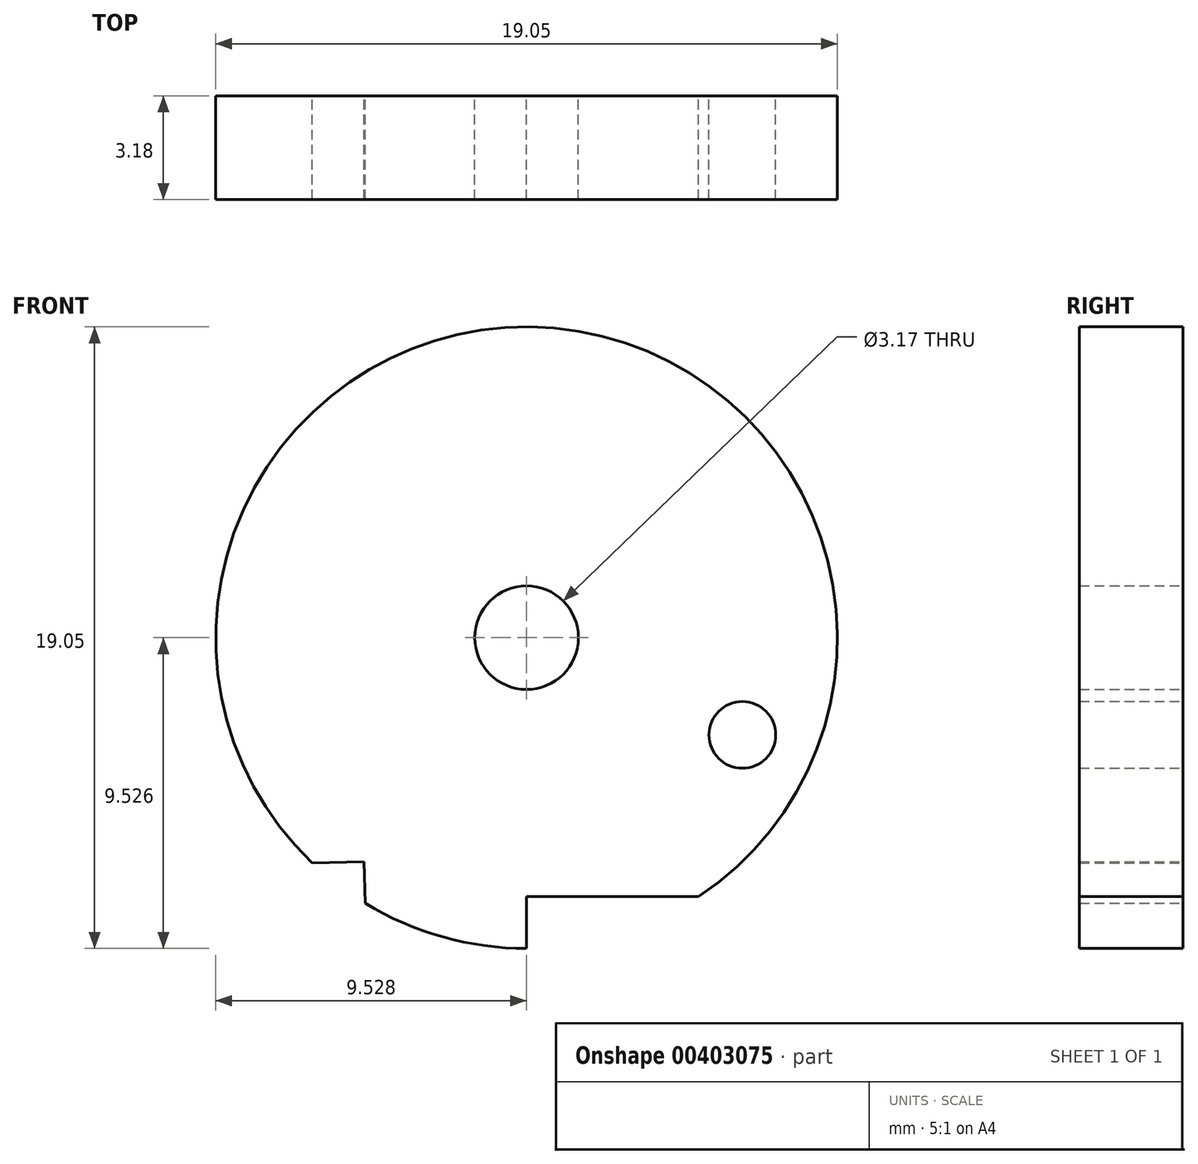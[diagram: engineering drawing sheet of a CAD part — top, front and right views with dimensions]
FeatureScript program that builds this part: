
annotation { "Feature Type Name" : "Feature", "Feature Type Description" : "" }
export const myFeature = defineFeature(function(context is Context, id is Id, definition is map)
    precondition{}
    {
        {
            var Q0;
            Q0=qCreatedBy(makeId("Front.planeOp"),FACE);
            var sketch = newSketch(context, id + "F0", { "sketchPlane" : qUnion([Q0])});
            skArc(sketch, "E0", {"start": v(-4.47, -3.05) * mm, "mid": v(-2.1, -4.09) * mm, "end": v(0.48, -4.44) * mm});
            skCircle(sketch, "E1", {"center": v(0.48, 5.09) * mm, "radius": 1.59 * mm});
            skLineSegment(sketch, "E2", {"start": v(-6.09, -1.81) * mm, "end": v(-4.5, -1.78) * mm});
            skLineSegment(sketch, "E3", {"start": v(-4.5, -1.78) * mm, "end": v(-4.47, -3.05) * mm});
            skCircle(sketch, "E4", {"center": v(7.09, 2.1) * mm, "radius": 1.02 * mm});
            skLineSegment(sketch, "E5", {"start": v(0.48, -2.85) * mm, "end": v(0.48, -4.44) * mm});
            skLineSegment(sketch, "E6", {"start": v(0.48, -2.85) * mm, "end": v(5.74, -2.85) * mm});
            skArc(sketch, "E7.trimOffspring", {"start": v(5.74, -2.85) * mm, "mid": v(1.31, 14.57) * mm, "end": v(-6.09, -1.81) * mm});
            skSolve(sketch);
        }
        {
            var Q0;
            Q0=makeQuery(id+"F0.imprint","IMPRINT",FACE,{"disambiguationData":[TD([[makeQuery(id+"F0.imprint","IMPRINT",EDGE,{"derivedFrom":sQuery(id+"F0.wireOp",EDGE,"E0")}),1.0]])]});
            extrude(context, id + "F1", {"entities" : qUnion([Q0]), "endBound" : BoundingType.SYMMETRIC, "depth" : 3.17 * mm});
        }
    });
